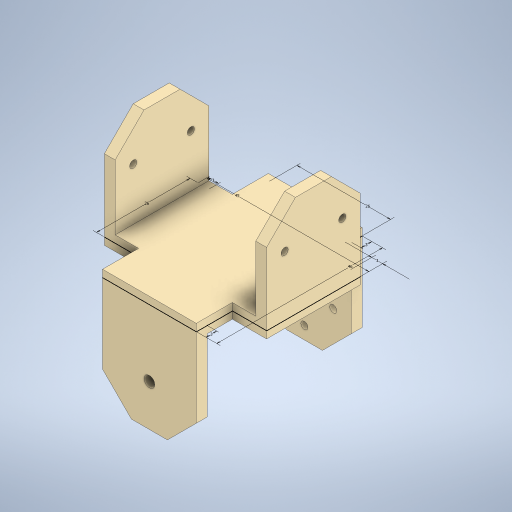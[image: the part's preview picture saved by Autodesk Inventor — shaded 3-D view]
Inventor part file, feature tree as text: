
AUTODESK INVENTOR PART (.ipt)
format: ipt  version: 2024 (Build 280153000, 153)  size: 360,960 bytes
history: native  units: in
note: dims shown in document units (in); Inventor stores cm internally (conversion verified against a paired STEP export)
features: extrude x10, sketch x6
ambient origin geometry x8: Origin, YZ Plane, XZ Plane, XY Plane, X Axis, Y Axis, Z Axis, Center Point
bodies: Solid1 (feature_tree)
feature tree (16):
  sketch  "Sketch1"  dims[d0=1.7717in d1=1.811in]
  extrude  "Extrusion1"  Depth=1.811in
  extrude  "Extrusion2"  Depth=1.0236in
  extrude  "Extrusion3"  Depth=0.1181in
  extrude  "Extrusion4"  Depth=0.1181in
  extrude  "Extrusion5"  Depth=1.1811in TaperAngle=0.0deg
  extrude  "Extrusion6"  Depth=0.0787in TaperAngle=0.0deg
  extrude  "Extrusion9"  Depth=0.0787in TaperAngle=0.0deg
  extrude  "Extrusion10"  Depth=0.0787in
  extrude  "Extrusion12"  Depth=0.0787in TaperAngle=0.0deg
  extrude  "Extrusion13"  Depth=0.0787in
  sketch  "Sketch2"  dims[d2=1.0236in d3=1.0236in]
  sketch  "Sketch6"  dims[d4=0.1181in d5=0.1181in]
  sketch  "Sketch7"  dims[d6=0.1181in d7=0.1181in]
  sketch  "Sketch9"  dims[d8=1.1024in d9=0.0in d10=1.1811in d11=0.0in]
  sketch  "Sketch10"  dims[d12=0.1575in d13=0.0in d14=0.0787in d15=0.0in d16=0.0787in d17=0.0in d18=0.4528in d26=2.3622in d27=0.0in d43=0.315in d44=0.315in d45=0.315in d46=0.315in d47=1.9685in d48=0.0in d49=0.315in d50=0.315in d51=0.315in d52=0.315in d53=1.9685in d54=0.0in d59=0.4528in d60=90.0deg d61=0.0787in d62=0.315in d63=1.5748in d65=360.0deg d67=0.1181in d68=0.0in d69=0.4528in d70=0.1181in d71=0.1181in d72=0.0in d73=0.0787in d74=0.315in d75=0.0197in d76=0.0344in d77=0.0197in d78=0.0344in]
